# Revit family: 687365B4E OPAL HAND SHOWER V JET BLACK BLACK FACE PLATE
name_source: partatom
category: Specialty Equipment
units: mm (PartAtom-declared; Revit-internal decimal feet)

## family parameters
Cut with Voids When Loaded = No
Host = Face
OmniClass Number = 23.45.05.14.17
OmniClass Title = Showers
Part Type = Normal
Room Calculation Point = No
Round Connector Dimension = Use Radius
Shared = No

## types (1)
- OPAL HAND SHOWER V JET BLACK BLACK FACE PLATE
    Assembly Code = D2010710
    Default Elevation = 1000 mm  [stored 3.28084 ft]
    Description = OPAL HAND SHOWER V JET BLACK BLACK FACE PLATE
    Manufacturer = GWA Bathrooms & Kitchens
    Material_Base = GWA-Metal-Black
    Material_Spray = GWA-Plastic-General
    Model = 687365B4E
    URL = https://www.caroma.com.au

note: [stored X ft] marks values corroborated as IEEE doubles in the binary element streams (Revit-internal decimal feet)

## geometry (parser evidence)
native form markers: Sweep x3
no freeform markers — native parametric forms only
